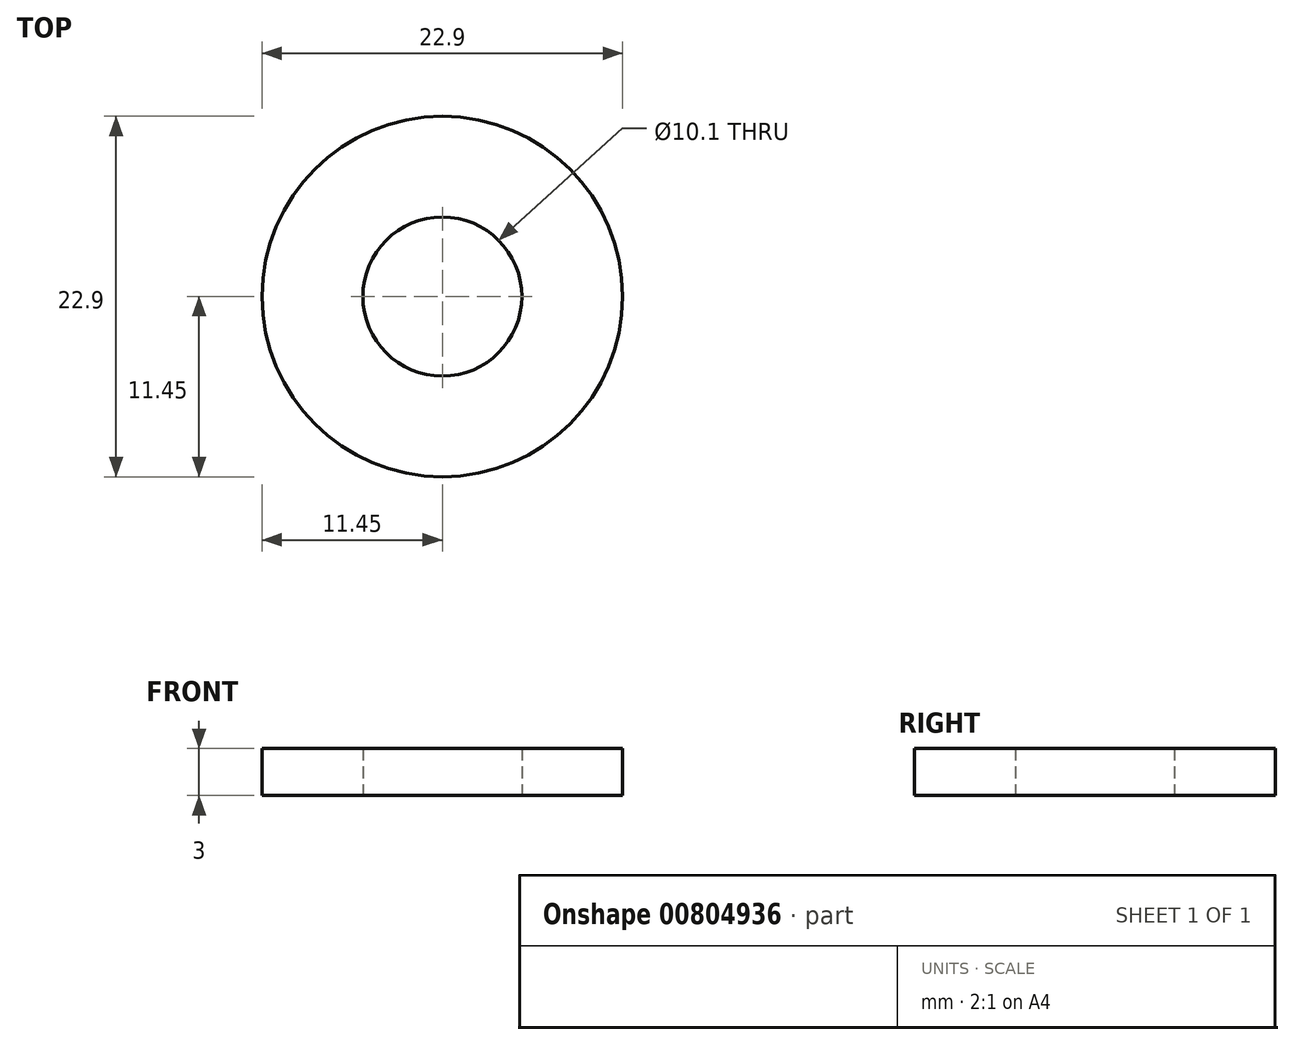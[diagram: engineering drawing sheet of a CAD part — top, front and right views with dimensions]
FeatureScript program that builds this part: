
annotation { "Feature Type Name" : "Feature", "Feature Type Description" : "" }
export const myFeature = defineFeature(function(context is Context, id is Id, definition is map)
    precondition{}
    {
        {
            var Q0;
            Q0=qCreatedBy(makeId("Top.planeOp"),FACE);
            var sketch = newSketch(context, id + "F0", { "sketchPlane" : qUnion([Q0])});
            skCircle(sketch, "E0", {"center": v(0, 0) * mm, "radius": 11.45 * mm});
            skCircle(sketch, "E1", {"center": v(0, 0) * mm, "radius": 5.05 * mm});
            skSolve(sketch);
        }
        {
            var Q0;
            Q0 = qSketchRegion(id + "F0", true);
            extrude(context, id + "F1", {"entities" : qUnion([Q0]), "depth" : 3 * mm, "offsetDistance" : 25 * mm});
        }
    });
